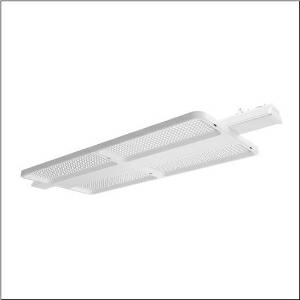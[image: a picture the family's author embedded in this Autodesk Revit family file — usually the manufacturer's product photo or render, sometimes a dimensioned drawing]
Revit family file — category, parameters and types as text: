
# Revit family: highbay_21_fur_licross_r__tragschiene_maxi_52hn12db4qla_5cb2
name_source: partatom
category: Lighting Fixtures
units: mm (PartAtom-declared; Revit-internal decimal feet)

## family parameters
Cut with Voids When Loaded = No
Host = Face
Light Source = No
Part Type = Normal
Room Calculation Point = No
Round Connector Dimension = Use Diameter
Shared = No

## types (1)
- --- (1 x LED, 38000 lm, 197.7 W, 4000K)
    Apparent Load = 198 VA
    CIE Flux Codes = 90 98 100 100 100
    Color Rendering = 80
    Color Temperature = 4000K
    Default Elevation = 1800 mm
    Description = Highbay 21 for Licross® trunking rail maxi, high bay luminaire, primary light control with lens, of PMMA, primary optical cover: cover, of PMMA, light emission: direct distribution, primary light characteristic: symmetric, LED, rated luminous flux: 38.000lm, luminous efficacy: 192lm/W, light colour: 840, colour temperature: 4000K, control gear: DALI 2, with plug, 5-pole, with phase selection, mains connection: 230..240V, AC, 50/60Hz, rated input power: 197.7W, housing frame, of high-performance plastic PA6, matt traffic white (RAL 9016), length: 1.250mm, width: 442mm, height: 71mm, lever catch, fixing on rail side, of steel, galvanised, white, blank cover, of PC/ABS, traffic white (RAL 9016), protection rating (complete): IP64, insulation class (complete): insulation class I (protective earthing), certification: CE, ENEC, VDE, UKCA, protection symbol: D, impact resistance: IK07, permissible operating ambient temperature: -40..+55°C, LABS conformity tested according to VDMA 24364:2018-05, corresponds to IFS (International Featured Standards) requirements for safety and quality in the food industry, packaging unit: 1 piece
    Height = 72 mm  [stored 0.23622 ft]
    Lamp = 1 x LED
    Lamp Light Flux = 38000 lm
    Lamp Power = 197.7 W
    Lamp count = 1
    Length = 946 mm
    Luminous efficacy = 192 lm/W
    Manufacturer = Siteco
    ModVariant = No
    Model = 52HN12DB4QLA
    Mounting Place = Ceiling
    Mounting Type = Pendant
    Number of Poles = 1
    OnlyDefault = Yes
    Power Factor = 1
    Product Name = Highbay 21 für Licross® Tragschiene maxi
    Product group = high bay luminaire
    ProductGroupID = 901
    Protection Class = Protection class I
    Protection Degree = IP 64
    RLX_Detail_Level = 1
    RLX_Emergency_Light_Flux = 0 lm
    RLX_Emergency_Type = 0
    RLX_Emergency_Type_DB = No
    RlxData = <blob elided: 24841 chars, md5=6d6acda9>
    Socket = socket
    Standby Power = 0 W
    System Light Flux = 38000 lm
    System Power = 198 W
    Type Comments = factory setting: luminous flux: 100 % | dim-lin: 254 | 918 mA
    Type Image = l_1361711.jpg
    URL = http://relux.com
    VarID = @adj_000433
    Voltage = 0 V
    Weight = 0.00 kg
    Width = 442 mm

note: [stored X ft] marks values corroborated as IEEE doubles in the binary element streams (Revit-internal decimal feet)

## geometry (parser evidence)
native form markers: Blend x4, Sweep x10
no freeform markers — native parametric forms only
